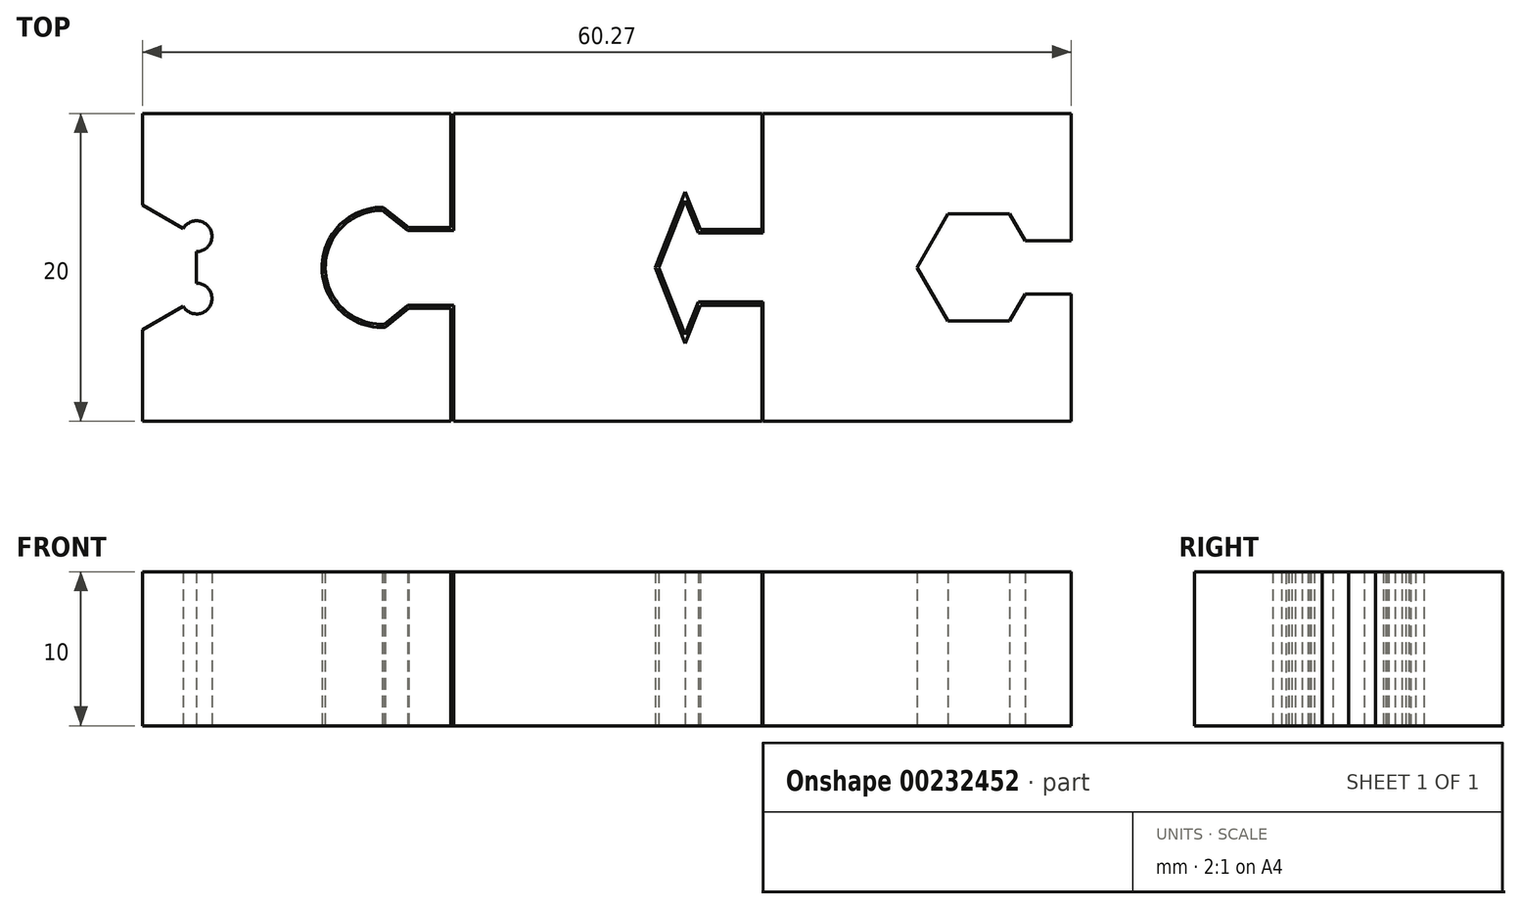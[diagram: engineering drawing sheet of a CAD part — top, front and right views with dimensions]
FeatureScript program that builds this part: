
annotation { "Feature Type Name" : "Feature", "Feature Type Description" : "" }
export const myFeature = defineFeature(function(context is Context, id is Id, definition is map)
    precondition{}
    {
        {
            var Q0;
            Q0=qCreatedBy(makeId("Top.planeOp"),FACE);
            var sketch = newSketch(context, id + "F0", { "sketchPlane" : qUnion([Q0])});
            skLineSegment(sketch, "E0.bottom", {"start": v(10, 10) * mm, "end": v(-10, 10) * mm});
            skLineSegment(sketch, "E0.top", {"start": v(10, -10) * mm, "end": v(-10, -10) * mm});
            skLineSegment(sketch, "E0.right", {"start": v(-10, 10) * mm, "end": v(-10, -10) * mm});
            skPoint(sketch, "E0.middle", {"position": v(0, 0) * mm});
            skLineSegment(sketch, "E1", {"start": v(-14.65, 3.7) * mm, "end": v(-10.74, 0.59) * mm});
            skLineSegment(sketch, "E2", {"start": v(-10, 0) * mm, "end": v(-14.65, 0) * mm});
            skLineSegment(sketch, "E3", {"start": v(-14.65, 0) * mm, "end": v(-14.65, 3.7) * mm});
            skLineSegment(sketch, "E4", {"start": v(-10.66, -0.54) * mm, "end": v(-14.53, -3.7) * mm});
            skArc(sketch, "E5", {"start": v(-14.65, 3.7) * mm, "mid": v(-18.35, -0.06) * mm, "end": v(-14.53, -3.7) * mm});
            skLineSegment(sketch, "E6", {"start": v(10, 10) * mm, "end": v(10, -10) * mm});
            skLineSegment(sketch, "E7", {"start": v(-13, -2.45) * mm, "end": v(-13, 0) * mm});
            skLineSegment(sketch, "E8", {"start": v(-13, 0) * mm, "end": v(-13, 2.39) * mm});
            skLineSegment(sketch, "E9", {"start": v(-13, 2.39) * mm, "end": v(-10, 2.39) * mm});
            skLineSegment(sketch, "E10", {"start": v(-13, -2.45) * mm, "end": v(-10, -2.45) * mm});
            skLineSegment(sketch, "E11", {"start": v(5, 0) * mm, "end": v(5, 4.9) * mm});
            skLineSegment(sketch, "E12", {"start": v(5, 4.9) * mm, "end": v(10, 4.9) * mm});
            skLineSegment(sketch, "E13", {"start": v(5, 0) * mm, "end": v(5, -4.93) * mm});
            skLineSegment(sketch, "E14", {"start": v(5, -4.93) * mm, "end": v(10, -4.93) * mm});
            skLineSegment(sketch, "E15", {"start": v(5, 4.9) * mm, "end": v(5, 0) * mm});
            skLineSegment(sketch, "E16", {"start": v(5, -4.93) * mm, "end": v(7, 0) * mm});
            skLineSegment(sketch, "E17", {"start": v(7, 0) * mm, "end": v(5, 4.9) * mm});
            skLineSegment(sketch, "E18", {"start": v(5, 4.9) * mm, "end": v(3.08, 0) * mm});
            skLineSegment(sketch, "E19", {"start": v(5, -4.93) * mm, "end": v(3.08, 0) * mm});
            skLineSegment(sketch, "E20", {"start": v(6, -2.46) * mm, "end": v(6, 2.45) * mm});
            skLineSegment(sketch, "E21", {"start": v(6, 2.45) * mm, "end": v(10, 2.45) * mm});
            skLineSegment(sketch, "E22", {"start": v(6, -2.46) * mm, "end": v(10, -2.46) * mm});
            skSolve(sketch);
        }
        {
            var Q0;
            {var subQ1=sQuery(id+"F0.wireOp",EDGE,"E3");Q0=makeQuery(id+"F0.imprint","IMPRINT",FACE,{"disambiguationData":[TD([[makeQuery(id+"F0.imprint","IMPRINT",EDGE,{"derivedFrom":subQ1}),1.0]])]});}
            var Q1;
            {var subQ0=sQuery(id+"F0.wireOp",EDGE,"E3");Q1=makeQuery(id+"F0.imprint","IMPRINT",FACE,{"disambiguationData":[TD([[makeQuery(id+"F0.imprint","IMPRINT",EDGE,{"derivedFrom":subQ0}),-1.0]])]});}
            var Q2;
            {var subQ3=sQuery(id+"F0.wireOp",EDGE,"E8");Q2=makeQuery(id+"F0.imprint","IMPRINT",FACE,{"disambiguationData":[TD([[makeQuery(id+"F0.imprint","IMPRINT",EDGE,{"derivedFrom":subQ3}),1.0]])]});}
            var Q3;
            {var subQ0=sQuery(id+"F0.wireOp",EDGE,"E7");Q3=makeQuery(id+"F0.imprint","IMPRINT",FACE,{"disambiguationData":[TD([[makeQuery(id+"F0.imprint","IMPRINT",EDGE,{"derivedFrom":subQ0}),1.0]])]});}
            var Q4;
            {var subQ3=sQuery(id+"F0.wireOp",EDGE,"E7");Q4=makeQuery(id+"F0.imprint","IMPRINT",FACE,{"disambiguationData":[TD([[makeQuery(id+"F0.imprint","IMPRINT",EDGE,{"derivedFrom":subQ3}),-1.0]])]});}
            var Q5;
            {var subQ3=sQuery(id+"F0.wireOp",EDGE,"E8");Q5=makeQuery(id+"F0.imprint","IMPRINT",FACE,{"disambiguationData":[TD([[makeQuery(id+"F0.imprint","IMPRINT",EDGE,{"derivedFrom":subQ3}),-1.0]])]});}
            var Q6;
            {var subQ3=sQuery(id+"F0.wireOp",EDGE,"E9");Q6=makeQuery(id+"F0.imprint","IMPRINT",FACE,{"disambiguationData":[TD([[makeQuery(id+"F0.imprint","IMPRINT",EDGE,{"derivedFrom":subQ3}),-1.0]])]});}
            var Q7;
            {var subQ3=sQuery(id+"F0.wireOp",EDGE,"E10");Q7=makeQuery(id+"F0.imprint","IMPRINT",FACE,{"disambiguationData":[TD([[makeQuery(id+"F0.imprint","IMPRINT",EDGE,{"derivedFrom":subQ3}),1.0]])]});}
            var Q8;
            {var subQ1=sQuery(id+"F0.wireOp",EDGE,"E0.bottom");Q8=makeQuery(id+"F0.imprint","IMPRINT",FACE,{"disambiguationData":[TD([[makeQuery(id+"F0.imprint","IMPRINT",EDGE,{"derivedFrom":subQ1}),1.0]])]});}
            var Q9;
            {var subQ0=sQuery(id+"F0.wireOp",EDGE,"E14");Q9=makeQuery(id+"F0.imprint","IMPRINT",FACE,{"disambiguationData":[TD([[makeQuery(id+"F0.imprint","IMPRINT",EDGE,{"derivedFrom":subQ0}),1.0]])]});}
            var Q10;
            {var subQ0=sQuery(id+"F0.wireOp",EDGE,"E12");Q10=makeQuery(id+"F0.imprint","IMPRINT",FACE,{"disambiguationData":[TD([[makeQuery(id+"F0.imprint","IMPRINT",EDGE,{"derivedFrom":subQ0}),-1.0]])]});}
            extrude(context, id + "F1", {"entities" : qUnion([Q0, Q1, Q2, Q3, Q4, Q5, Q6, Q7, Q8, Q9, Q10]), "depth" : 10 * mm});
        }
        {
            var Q0;
            Q0=qCreatedBy(makeId("Top.planeOp"),FACE);
            var sketch = newSketch(context, id + "F2", { "sketchPlane" : qUnion([Q0])});
            skLineSegment(sketch, "E23.bottom", {"start": v(10.07, 10) * mm, "end": v(30.07, 10) * mm});
            skLineSegment(sketch, "E23.top", {"start": v(10.07, -10) * mm, "end": v(30.07, -10) * mm});
            skLineSegment(sketch, "E23.left", {"start": v(10.07, 10) * mm, "end": v(10.07, -10) * mm});
            skLineSegment(sketch, "E24", {"start": v(30.07, 10) * mm, "end": v(30.07, 1.73) * mm});
            skLineSegment(sketch, "E25.cCircle", {"start": v(27.07, 1.73) * mm, "end": v(27.07, 1.73) * mm});
            skLineSegment(sketch, "E25.0", {"start": v(22.07, 3.46) * mm, "end": v(26.07, 3.46) * mm});
            skLineSegment(sketch, "E25.1", {"start": v(26.07, 3.46) * mm, "end": v(27.07, 1.73) * mm});
            skLineSegment(sketch, "E25.2", {"start": v(27.07, -1.73) * mm, "end": v(26.07, -3.46) * mm});
            skLineSegment(sketch, "E25.3", {"start": v(26.07, -3.46) * mm, "end": v(22.07, -3.46) * mm});
            skLineSegment(sketch, "E25.4", {"start": v(22.07, -3.46) * mm, "end": v(20.07, 0) * mm});
            skLineSegment(sketch, "E25.5", {"start": v(20.07, 0) * mm, "end": v(22.07, 3.46) * mm});
            skPoint(sketch, "E25.0.midPoint", {"position": v(24.07, 3.46) * mm});
            skLineSegment(sketch, "E26.bottom", {"start": v(27.07, -1.73) * mm, "end": v(30.07, -1.73) * mm});
            skLineSegment(sketch, "E26.top", {"start": v(27.07, 1.73) * mm, "end": v(30.07, 1.73) * mm});
            skPoint(sketch, "E26.middle", {"position": v(28.07, 0) * mm});
            skLineSegment(sketch, "E27.trimOffspring", {"start": v(30.07, -1.73) * mm, "end": v(30.07, -10) * mm});
            skLineSegment(sketch, "E28.trimOffspring", {"start": v(27.07, -1.73) * mm, "end": v(27.07, -1.73) * mm});
            skPoint(sketch, "E29.orphan", {"position": v(26.07, -1.73) * mm});
            skPoint(sketch, "E30.orphan", {"position": v(26.07, 1.73) * mm});
            skLineSegment(sketch, "E31", {"start": v(10.07, 1.54) * mm, "end": v(10.07, -2.46) * mm});
            skLineSegment(sketch, "E32.bottom", {"start": v(10.07, -2.25) * mm, "end": v(4.57, -2.25) * mm});
            skLineSegment(sketch, "E32.top", {"start": v(10.07, 2.25) * mm, "end": v(4.57, 2.25) * mm});
            skLineSegment(sketch, "E32.left", {"start": v(10.07, -2.25) * mm, "end": v(10.07, 2.25) * mm});
            skLineSegment(sketch, "E32.right", {"start": v(4.57, -2.25) * mm, "end": v(4.57, 2.25) * mm});
            skPoint(sketch, "E32.middle", {"position": v(7.32, 0) * mm});
            skLineSegment(sketch, "E33", {"start": v(5.01, -4.36) * mm, "end": v(5.87, -2.25) * mm});
            skLineSegment(sketch, "E34", {"start": v(3.3, 0) * mm, "end": v(5.01, -4.36) * mm});
            skLineSegment(sketch, "E35", {"start": v(3.3, 0) * mm, "end": v(5.01, 4.33) * mm});
            skLineSegment(sketch, "E36", {"start": v(5.01, 4.33) * mm, "end": v(5.87, 2.25) * mm});
            skSolve(sketch);
        }
        {
            var Q0;
            {var subQ3=sQuery(id+"F0.wireOp",EDGE,"E0.bottom");Q0=makeQuery(id+"F0.imprint","IMPRINT",FACE,{"disambiguationData":[TD([[makeQuery(id+"F0.imprint","IMPRINT",EDGE,{"derivedFrom":subQ3}),1.0]])]});}
            var sketch = newSketch(context, id + "F3", { "sketchPlane" : qUnion([Q0])});
            skPoint(sketch, "E37.trimOffspring.end.orphan", {"position": v(-10.74, 0.59) * mm});
            skPoint(sketch, "E38.orphan", {"position": v(-10.66, -0.54) * mm});
            skPoint(sketch, "E39.0.end.orphan", {"position": v(-14.53, -3.7) * mm});
            skPoint(sketch, "E39.0.start.orphan", {"position": v(-14.65, 3.7) * mm});
            skPoint(sketch, "E40.orphan", {"position": v(-13, 2.39) * mm});
            skPoint(sketch, "E41.orphan", {"position": v(-13, -2.45) * mm});
            skArc(sketch, "E42.0", {"start": v(-14.58, 3.9) * mm, "mid": v(-18.55, -0.06) * mm, "end": v(-14.45, -3.9) * mm});
            skLineSegment(sketch, "E43.0", {"start": v(-14.58, 3.9) * mm, "end": v(-12.93, 2.59) * mm});
            skLineSegment(sketch, "E44.0", {"start": v(-12.93, -2.65) * mm, "end": v(-14.45, -3.9) * mm});
            skLineSegment(sketch, "E45.0", {"start": v(-12.93, 2.59) * mm, "end": v(-10.2, 2.59) * mm});
            skLineSegment(sketch, "E46.0", {"start": v(-12.93, -2.65) * mm, "end": v(-10.2, -2.65) * mm});
            skLineSegment(sketch, "E47.0", {"start": v(-10.2, 10) * mm, "end": v(-10.2, 2.59) * mm});
            skLineSegment(sketch, "E48.trimOffspring", {"start": v(-10.2, -2.65) * mm, "end": v(-10.2, -10) * mm});
            skLineSegment(sketch, "E49", {"start": v(-10.2, -10) * mm, "end": v(-30.2, -10) * mm});
            skLineSegment(sketch, "E50", {"start": v(-30.2, -10) * mm, "end": v(-30.2, 10) * mm});
            skLineSegment(sketch, "E51", {"start": v(-10.2, 10) * mm, "end": v(-30.2, 10) * mm});
            skSolve(sketch);
        }
        {
            var Q0;
            Q0=qSketchRegion(id+"F2",true);
            extrude(context, id + "F4", {"entities" : qUnion([Q0]), "depth" : 10 * mm});
        }
        {
            var Q0;
            Q0=makeQuery(id+"F3.imprint","IMPRINT",FACE,{"disambiguationData":[TD([[makeQuery(id+"F3.imprint","IMPRINT",EDGE,{"derivedFrom":sQuery(id+"F3.wireOp",EDGE,"E42.0")}),-1.0]])]});
            var Q1;
            Q1=makeQuery(id+"F1.opExtrude","CAP_FACE",FACE,{"disambiguationData":[OSD([sQuery(id+"F0.wireOp",EDGE,"E0.bottom"),sQuery(id+"F0.wireOp",EDGE,"E0.top"),sQuery(id+"F0.wireOp",EDGE,"E0.right"),sQuery(id+"F0.wireOp",EDGE,"E1"),sQuery(id+"F0.wireOp",EDGE,"E4"),sQuery(id+"F0.wireOp",EDGE,"E5"),sQuery(id+"F0.wireOp",EDGE,"E6"),sQuery(id+"F0.wireOp",EDGE,"E9"),sQuery(id+"F0.wireOp",EDGE,"E10"),sQuery(id+"F0.wireOp",EDGE,"E16"),sQuery(id+"F0.wireOp",EDGE,"E17"),sQuery(id+"F0.wireOp",EDGE,"E18"),sQuery(id+"F0.wireOp",EDGE,"E19"),sQuery(id+"F0.wireOp",EDGE,"E21"),sQuery(id+"F0.wireOp",EDGE,"E22")])],"isStart":false});
            extrude(context, id + "F5", {"entities" : qUnion([Q0]), "endBound" : BoundingType.UP_TO_SURFACE, "endBoundEntityFace" : qUnion([Q1]), "depth" : 25 * mm});
        }
        {
            var Q0;
            Q0=makeQuery(id+"F5.opExtrude","CAP_FACE",FACE,{"disambiguationData":[OSD([sQuery(id+"F3.wireOp",EDGE,"E42.0"),sQuery(id+"F3.wireOp",EDGE,"E43.0"),sQuery(id+"F3.wireOp",EDGE,"E44.0"),sQuery(id+"F3.wireOp",EDGE,"E45.0"),sQuery(id+"F3.wireOp",EDGE,"E46.0"),sQuery(id+"F3.wireOp",EDGE,"E47.0"),sQuery(id+"F3.wireOp",EDGE,"E48.trimOffspring"),sQuery(id+"F3.wireOp",EDGE,"E49"),sQuery(id+"F3.wireOp",EDGE,"E50"),sQuery(id+"F3.wireOp",EDGE,"E51")])],"isStart":false});
            var sketch = newSketch(context, id + "F6", { "sketchPlane" : qUnion([Q0])});
            skCircle(sketch, "E52.cCircle", {"center": v(-30.2, 0) * mm, "radius": 3.5 * mm, "construction": true});
            skPoint(sketch, "E52.cCircle.perimeterSnap0", {"position": v(-30.2, 0) * mm});
            skLineSegment(sketch, "E52.0", {"start": v(-26.7, 2.02) * mm, "end": v(-26.7, -2.02) * mm});
            skLineSegment(sketch, "E52.1", {"start": v(-26.7, -2.02) * mm, "end": v(-30.2, -4.04) * mm});
            skLineSegment(sketch, "E52.2", {"start": v(-30.2, -4.04) * mm, "end": v(-33.7, -2.02) * mm});
            skLineSegment(sketch, "E52.3", {"start": v(-33.7, -2.02) * mm, "end": v(-33.7, 2.02) * mm});
            skLineSegment(sketch, "E52.4", {"start": v(-33.7, 2.02) * mm, "end": v(-30.2, 4.04) * mm});
            skLineSegment(sketch, "E52.5", {"start": v(-30.2, 4.04) * mm, "end": v(-26.7, 2.02) * mm});
            skPoint(sketch, "E52.0.midPoint", {"position": v(-26.7, 0) * mm});
            skPoint(sketch, "E52.0.midPoint.positionSnap0", {"position": v(-30.2, 0) * mm});
            skSolve(sketch);
        }
        {
            var Q0;
            Q0=qSketchRegion(id+"F6",true);
            extrude(context, id + "F7", {"entities" : qUnion([Q0]), "operationType" : NewBodyOperationType.REMOVE, "endBound" : BoundingType.THROUGH_ALL, "oppositeDirection" : true, "depth" : 25 * mm});
        }
        {
            var Q0;
            Q0=makeQuery(id+"F5.opExtrude","CAP_FACE",FACE,{"disambiguationData":[OSD([sQuery(id+"F3.wireOp",EDGE,"E42.0"),sQuery(id+"F3.wireOp",EDGE,"E43.0"),sQuery(id+"F3.wireOp",EDGE,"E44.0"),sQuery(id+"F3.wireOp",EDGE,"E45.0"),sQuery(id+"F3.wireOp",EDGE,"E46.0"),sQuery(id+"F3.wireOp",EDGE,"E47.0"),sQuery(id+"F3.wireOp",EDGE,"E48.trimOffspring"),sQuery(id+"F3.wireOp",EDGE,"E49"),sQuery(id+"F3.wireOp",EDGE,"E50"),sQuery(id+"F3.wireOp",EDGE,"E51")])],"isStart":true});
            var sketch = newSketch(context, id + "F8", { "sketchPlane" : qUnion([Q0])});
            skCircle(sketch, "E53", {"center": v(-26.7, -2.02) * mm, "radius": 1 * mm});
            skCircle(sketch, "E54", {"center": v(-26.7, 2.02) * mm, "radius": 1 * mm});
            skSolve(sketch);
        }
        {
            var Q0;
            Q0=qSketchRegion(id+"F8",true);
            extrude(context, id + "F9", {"entities" : qUnion([Q0]), "operationType" : NewBodyOperationType.REMOVE, "endBound" : BoundingType.THROUGH_ALL, "oppositeDirection" : true, "depth" : 25 * mm});
        }
    });
